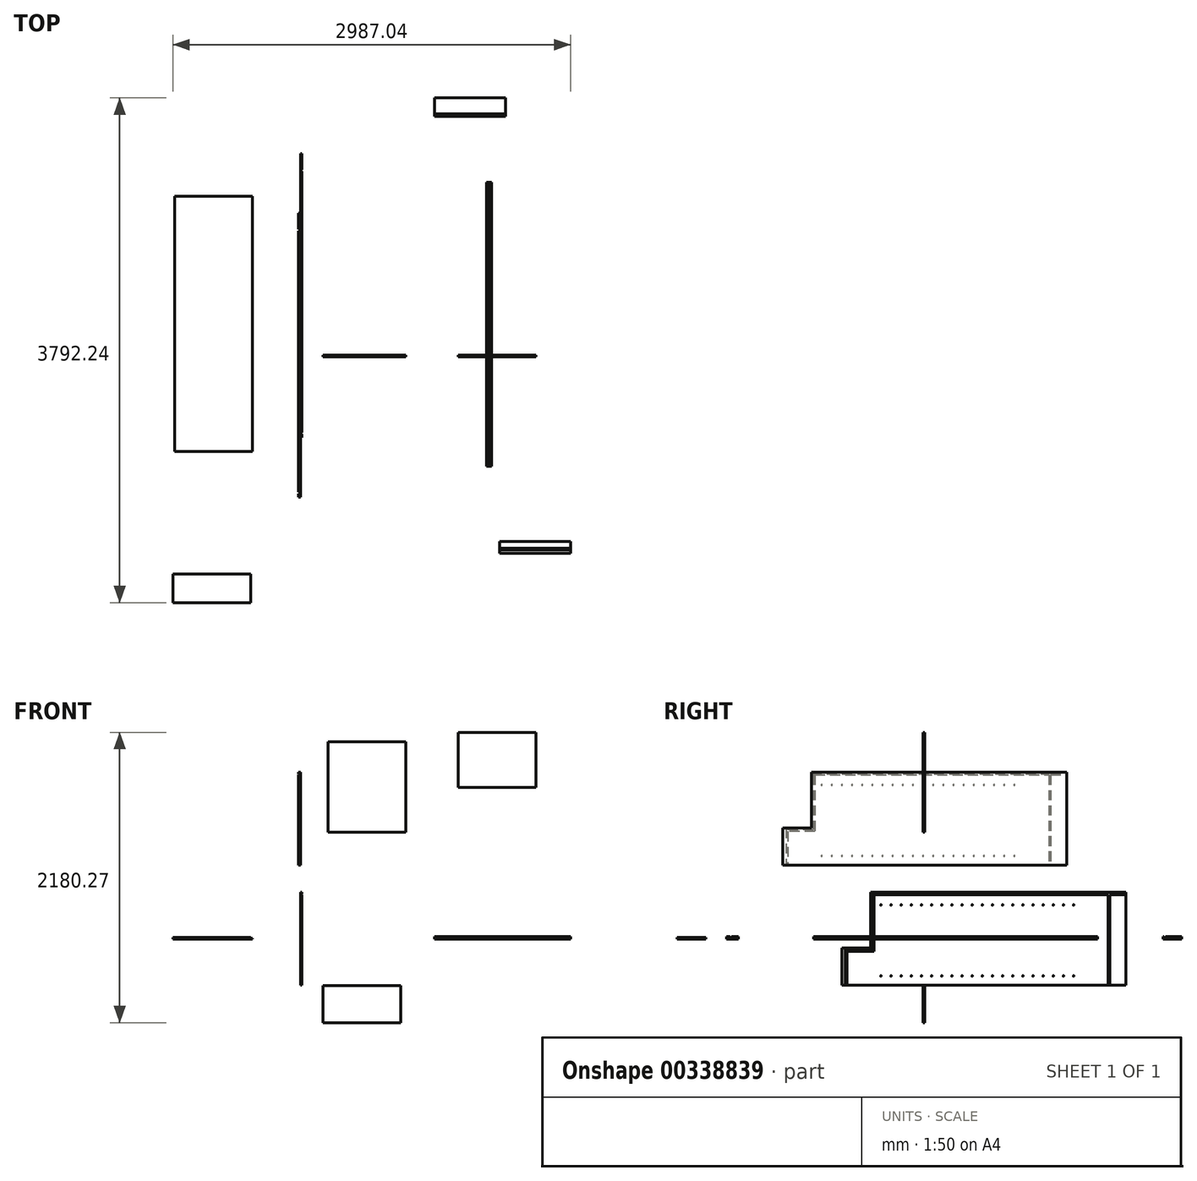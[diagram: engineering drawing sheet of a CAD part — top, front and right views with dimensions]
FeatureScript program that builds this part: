
annotation { "Feature Type Name" : "Feature", "Feature Type Description" : "" }
export const myFeature = defineFeature(function(context is Context, id is Id, definition is map)
    precondition{}
    {
        {
            var Q0;
            Q0=qCreatedBy(makeId("Right.planeOp"),FACE);
            var sketch = newSketch(context, id + "F0", { "sketchPlane" : qUnion([Q0])});
            skLineSegment(sketch, "E0.bottom", {"start": v(-620.38, -346.81) * mm, "end": v(1513.22, -346.81) * mm});
            skLineSegment(sketch, "E0.top", {"start": v(-620.38, 351.69) * mm, "end": v(1513.22, 351.69) * mm});
            skLineSegment(sketch, "E0.left", {"start": v(-620.38, -346.81) * mm, "end": v(-620.38, 351.69) * mm});
            skLineSegment(sketch, "E0.right", {"start": v(1513.22, -346.81) * mm, "end": v(1513.22, 351.69) * mm});
            skSolve(sketch);
        }
        {
            var Q0;
            Q0 = qSketchRegion(id + "F0", true);
            extrude(context, id + "F1", {"entities" : qUnion([Q0]), "depth" : 12.7 * mm});
        }
        {
            var Q0;
            Q0=makeQuery(id+"F1.opExtrude","CAP_FACE",FACE,{"disambiguationData":[OSD([sQuery(id+"F0.wireOp",EDGE,"E0.bottom"),sQuery(id+"F0.wireOp",EDGE,"E0.top"),sQuery(id+"F0.wireOp",EDGE,"E0.left"),sQuery(id+"F0.wireOp",EDGE,"E0.right")])],"isStart":false});
            var sketch = newSketch(context, id + "F2", { "sketchPlane" : qUnion([Q0])});
            skLineSegment(sketch, "E1.0", {"start": v(-620.38, 332.64) * mm, "end": v(1513.22, 332.64) * mm});
            skLineSegment(sketch, "E2.0", {"start": v(-620.38, 338.99) * mm, "end": v(1513.22, 338.99) * mm});
            skLineSegment(sketch, "E3.0", {"start": v(-594.98, -346.81) * mm, "end": v(-594.98, 351.69) * mm});
            skLineSegment(sketch, "E4.0", {"start": v(-582.28, -346.81) * mm, "end": v(-582.28, 351.69) * mm});
            skLineSegment(sketch, "E5.0", {"start": v(1379.87, -346.81) * mm, "end": v(1379.87, 351.69) * mm});
            skLineSegment(sketch, "E6.0", {"start": v(1392.57, -346.81) * mm, "end": v(1392.57, 351.69) * mm});
            skSolve(sketch);
        }
        {
            var Q0;
            Q0 = qSketchRegion(id + "F2", true);
            var Q1;
            {var subQ0=sQuery(id+"F2.wireOp",EDGE,"E5.0");var subQ1=sQuery(id+"F2.wireOp",EDGE,"E2.0");var subQ2=makeQuery(id+"F2.imprint","INTERSECT",VERTEX,{"derivedFrom":[subQ1,subQ0]});Q1=makeQuery(id+"F2.imprint","IMPRINT",FACE,{"disambiguationData":[TD([[makeQuery(id+"F2.imprint","IMPRINT",EDGE,{"disambiguationData":[TD([[subQ2,-1.0]])],"derivedFrom":subQ1}),1.0]])]});}
            var Q2;
            {var subQ0=sQuery(id+"F2.wireOp",EDGE,"E1.0");var subQ1=makeQuery(id+"F1.opExtrude","CAP_EDGE",EDGE,{"disambiguationData":[OSD([sQuery(id+"F0.wireOp",EDGE,"E0.right")])],"isStart":false});var subQ2=makeQuery(id+"F2.imprint","INTERSECT",VERTEX,{"derivedFrom":[subQ1,subQ0]});Q2=makeQuery(id+"F2.imprint","IMPRINT",FACE,{"disambiguationData":[TD([[makeQuery(id+"F2.imprint","IMPRINT",EDGE,{"disambiguationData":[TD([[subQ2,1.0]])],"derivedFrom":subQ0}),1.0]])]});}
            var Q3;
            {var subQ0=sQuery(id+"F2.wireOp",EDGE,"E3.0");var subQ1=sQuery(id+"F2.wireOp",EDGE,"E2.0");var subQ2=makeQuery(id+"F2.imprint","INTERSECT",VERTEX,{"derivedFrom":[subQ1,subQ0]});Q3=makeQuery(id+"F2.imprint","IMPRINT",FACE,{"disambiguationData":[TD([[makeQuery(id+"F2.imprint","IMPRINT",EDGE,{"disambiguationData":[TD([[subQ2,-1.0]])],"derivedFrom":subQ1}),1.0]])]});}
            var Q4;
            {var subQ0=sQuery(id+"F2.wireOp",EDGE,"E1.0");var subQ1=makeQuery(id+"F1.opExtrude","CAP_EDGE",EDGE,{"disambiguationData":[OSD([sQuery(id+"F0.wireOp",EDGE,"E0.left")])],"isStart":false});var subQ2=makeQuery(id+"F2.imprint","INTERSECT",VERTEX,{"derivedFrom":[subQ1,subQ0]});Q4=makeQuery(id+"F2.imprint","IMPRINT",FACE,{"disambiguationData":[TD([[makeQuery(id+"F2.imprint","IMPRINT",EDGE,{"disambiguationData":[TD([[subQ2,-1.0]])],"derivedFrom":subQ0}),1.0]])]});}
            var Q5;
            {var subQ0=sQuery(id+"F2.wireOp",EDGE,"E3.0");var subQ1=sQuery(id+"F2.wireOp",EDGE,"E1.0");var subQ2=makeQuery(id+"F2.imprint","INTERSECT",VERTEX,{"derivedFrom":[subQ1,subQ0]});Q5=makeQuery(id+"F2.imprint","IMPRINT",FACE,{"disambiguationData":[TD([[makeQuery(id+"F2.imprint","IMPRINT",EDGE,{"disambiguationData":[TD([[subQ2,-1.0]])],"derivedFrom":subQ1}),-1.0]])]});}
            var Q6;
            {var subQ0=sQuery(id+"F2.wireOp",EDGE,"E5.0");var subQ1=sQuery(id+"F2.wireOp",EDGE,"E1.0");var subQ2=makeQuery(id+"F2.imprint","INTERSECT",VERTEX,{"derivedFrom":[subQ1,subQ0]});Q6=makeQuery(id+"F2.imprint","IMPRINT",FACE,{"disambiguationData":[TD([[makeQuery(id+"F2.imprint","IMPRINT",EDGE,{"disambiguationData":[TD([[subQ2,-1.0]])],"derivedFrom":subQ1}),-1.0]])]});}
            extrude(context, id + "F3", {"entities" : qUnion([Q0, Q1, Q2, Q3, Q4, Q5, Q6]), "operationType" : NewBodyOperationType.REMOVE, "oppositeDirection" : true, "depth" : 6.35 * mm});
        }
        {
            var Q0;
            {var subQ0=sQuery(id+"F0.wireOp",EDGE,"E0.top");var subQ1=sQuery(id+"F2.wireOp",EDGE,"E4.0");var subQ2=sQuery(id+"F2.wireOp",EDGE,"E2.0");var subQ3=makeQuery(id+"F2.imprint","INTERSECT",VERTEX,{"derivedFrom":[subQ2,subQ1]});Q0=makeQuery(id+"F3.boolean.opBoolean","SPLIT",FACE,{"disambiguationData":[TD([makeQuery(id+"F3.opExtrude","SWEPT_FACE",FACE,{"disambiguationData":[OSD([subQ2]),TDD([makeQuery(id+"F2.imprint","IMPRINT",EDGE,{"disambiguationData":[TD([[subQ3,-1.0]])],"derivedFrom":subQ2})])]})])],"derivedFrom":makeQuery(id+"F1.opExtrude","CAP_FACE",FACE,{"disambiguationData":[OSD([sQuery(id+"F0.wireOp",EDGE,"E0.bottom"),subQ0,sQuery(id+"F0.wireOp",EDGE,"E0.left"),sQuery(id+"F0.wireOp",EDGE,"E0.right")])],"isStart":false})});}
            var sketch = newSketch(context, id + "F4", { "sketchPlane" : qUnion([Q0])});
            skLineSegment(sketch, "E7.0", {"start": v(-582.28, 415.19) * mm, "end": v(1379.87, 415.19) * mm, "construction": true});
            skLineSegment(sketch, "E8.0", {"start": v(-328.28, -327.76) * mm, "end": v(-328.28, 351.69) * mm, "construction": true});
            skCircle(sketch, "E9", {"center": v(-328.28, 415.19) * mm, "radius": 3.17 * mm});
            skCircle(sketch, "E10.0.1.0", {"center": v(-328.28, 948.59) * mm, "radius": 3.17 * mm});
            skCircle(sketch, "E10.1.0.0", {"center": v(-252.08, 415.19) * mm, "radius": 3.17 * mm});
            skCircle(sketch, "E10.1.1.0", {"center": v(-252.08, 948.59) * mm, "radius": 3.17 * mm});
            skCircle(sketch, "E10.2.0.0", {"center": v(-175.88, 415.19) * mm, "radius": 3.17 * mm});
            skCircle(sketch, "E10.2.1.0", {"center": v(-175.88, 948.59) * mm, "radius": 3.17 * mm});
            skCircle(sketch, "E10.3.0.0", {"center": v(-99.68, 415.19) * mm, "radius": 3.17 * mm});
            skCircle(sketch, "E10.3.1.0", {"center": v(-99.68, 948.59) * mm, "radius": 3.17 * mm});
            skCircle(sketch, "E10.4.0.0", {"center": v(-23.48, 415.19) * mm, "radius": 3.17 * mm});
            skCircle(sketch, "E10.4.1.0", {"center": v(-23.48, 948.59) * mm, "radius": 3.17 * mm});
            skCircle(sketch, "E10.5.0.0", {"center": v(52.72, 415.19) * mm, "radius": 3.17 * mm});
            skCircle(sketch, "E10.5.1.0", {"center": v(52.72, 948.59) * mm, "radius": 3.17 * mm});
            skCircle(sketch, "E10.6.0.0", {"center": v(128.92, 415.19) * mm, "radius": 3.17 * mm});
            skCircle(sketch, "E10.6.1.0", {"center": v(128.92, 948.59) * mm, "radius": 3.17 * mm});
            skCircle(sketch, "E10.7.0.0", {"center": v(205.12, 415.19) * mm, "radius": 3.17 * mm});
            skCircle(sketch, "E10.7.1.0", {"center": v(205.12, 948.59) * mm, "radius": 3.17 * mm});
            skCircle(sketch, "E10.8.0.0", {"center": v(281.32, 415.19) * mm, "radius": 3.17 * mm});
            skCircle(sketch, "E10.8.1.0", {"center": v(281.32, 948.59) * mm, "radius": 3.17 * mm});
            skCircle(sketch, "E10.9.0.0", {"center": v(357.52, 415.19) * mm, "radius": 3.17 * mm});
            skCircle(sketch, "E10.9.1.0", {"center": v(357.52, 948.59) * mm, "radius": 3.17 * mm});
            skCircle(sketch, "E10.10.0.0", {"center": v(433.72, 415.19) * mm, "radius": 3.17 * mm});
            skCircle(sketch, "E10.10.1.0", {"center": v(433.72, 948.59) * mm, "radius": 3.17 * mm});
            skCircle(sketch, "E10.11.0.0", {"center": v(509.92, 415.19) * mm, "radius": 3.17 * mm});
            skCircle(sketch, "E10.11.1.0", {"center": v(509.92, 948.59) * mm, "radius": 3.17 * mm});
            skCircle(sketch, "E10.12.0.0", {"center": v(586.12, 415.19) * mm, "radius": 3.17 * mm});
            skCircle(sketch, "E10.12.1.0", {"center": v(586.12, 948.59) * mm, "radius": 3.17 * mm});
            skCircle(sketch, "E10.13.0.0", {"center": v(662.32, 415.19) * mm, "radius": 3.17 * mm});
            skCircle(sketch, "E10.13.1.0", {"center": v(662.32, 948.59) * mm, "radius": 3.17 * mm});
            skCircle(sketch, "E10.14.0.0", {"center": v(738.52, 415.19) * mm, "radius": 3.17 * mm});
            skCircle(sketch, "E10.14.1.0", {"center": v(738.52, 948.59) * mm, "radius": 3.17 * mm});
            skCircle(sketch, "E10.15.0.0", {"center": v(814.72, 415.19) * mm, "radius": 3.17 * mm});
            skCircle(sketch, "E10.15.1.0", {"center": v(814.72, 948.59) * mm, "radius": 3.17 * mm});
            skCircle(sketch, "E10.16.0.0", {"center": v(890.92, 415.19) * mm, "radius": 3.17 * mm});
            skCircle(sketch, "E10.16.1.0", {"center": v(890.92, 948.59) * mm, "radius": 3.17 * mm});
            skCircle(sketch, "E10.17.0.0", {"center": v(967.12, 415.19) * mm, "radius": 3.17 * mm});
            skCircle(sketch, "E10.17.1.0", {"center": v(967.12, 948.59) * mm, "radius": 3.17 * mm});
            skCircle(sketch, "E10.18.0.0", {"center": v(1043.32, 415.19) * mm, "radius": 3.17 * mm});
            skCircle(sketch, "E10.18.1.0", {"center": v(1043.32, 948.59) * mm, "radius": 3.17 * mm});
            skCircle(sketch, "E10.19.0.0", {"center": v(1119.52, 415.19) * mm, "radius": 3.17 * mm});
            skCircle(sketch, "E10.19.1.0", {"center": v(1119.52, 948.59) * mm, "radius": 3.17 * mm});
            skLineSegment(sketch, "E10.direction1", {"start": v(-328.28, 415.19) * mm, "end": v(-252.08, 415.19) * mm, "construction": true});
            skLineSegment(sketch, "E10.direction2", {"start": v(-328.28, 415.19) * mm, "end": v(-328.28, 948.59) * mm, "construction": true});
            skSolve(sketch);
        }
        {
            var Q0;
            Q0 = qSketchRegion(id + "F4", true);
            extrude(context, id + "F5", {"entities" : qUnion([Q0]), "operationType" : NewBodyOperationType.REMOVE, "oppositeDirection" : true, "depth" : 9.52 * mm});
        }
        {
            var Q0;
            Q0=makeQuery(id+"F1.opExtrude","CAP_FACE",FACE,{"disambiguationData":[OSD([sQuery(id+"F0.wireOp",EDGE,"E0.bottom"),sQuery(id+"F0.wireOp",EDGE,"E0.top"),sQuery(id+"F0.wireOp",EDGE,"E0.left"),sQuery(id+"F0.wireOp",EDGE,"E0.right")])],"isStart":true});
            var sketch = newSketch(context, id + "F6", { "sketchPlane" : qUnion([Q0])});
            skLineSegment(sketch, "E11.bottom", {"start": v(1065.98, 1252.71) * mm, "end": v(-1067.62, 1252.71) * mm});
            skLineSegment(sketch, "E11.top", {"start": v(1065.98, 554.21) * mm, "end": v(-1067.62, 554.21) * mm});
            skLineSegment(sketch, "E11.left", {"start": v(1065.98, 1252.71) * mm, "end": v(1065.98, 554.21) * mm});
            skLineSegment(sketch, "E11.right", {"start": v(-1067.62, 1252.71) * mm, "end": v(-1067.62, 554.21) * mm});
            skSolve(sketch);
        }
        {
            var Q0;
            Q0 = qSketchRegion(id + "F6", true);
            extrude(context, id + "F7", {"entities" : qUnion([Q0]), "depth" : 12.7 * mm});
        }
        {
            var Q0;
            Q0=makeQuery(id+"F7.opExtrude","CAP_FACE",FACE,{"disambiguationData":[OSD([sQuery(id+"F6.wireOp",EDGE,"E11.bottom"),sQuery(id+"F6.wireOp",EDGE,"E11.top"),sQuery(id+"F6.wireOp",EDGE,"E11.left"),sQuery(id+"F6.wireOp",EDGE,"E11.right")])],"isStart":false});
            var sketch = newSketch(context, id + "F8", { "sketchPlane" : qUnion([Q0])});
            skLineSegment(sketch, "E12.0", {"start": v(1065.98, 1240.01) * mm, "end": v(-1067.62, 1240.01) * mm});
            skLineSegment(sketch, "E13.0", {"start": v(1065.98, 1233.66) * mm, "end": v(-1067.62, 1233.66) * mm});
            skLineSegment(sketch, "E14.0", {"start": v(-934.27, 1252.71) * mm, "end": v(-934.27, 554.21) * mm});
            skLineSegment(sketch, "E15.0", {"start": v(-946.97, 1252.71) * mm, "end": v(-946.97, 554.21) * mm});
            skLineSegment(sketch, "E16.0", {"start": v(1040.58, 1252.71) * mm, "end": v(1040.58, 554.21) * mm});
            skLineSegment(sketch, "E17.0", {"start": v(1027.88, 1252.71) * mm, "end": v(1027.88, 554.21) * mm});
            skSolve(sketch);
        }
        {
            var Q0;
            {var subQ0=sQuery(id+"F8.wireOp",EDGE,"E16.0");var subQ1=sQuery(id+"F8.wireOp",EDGE,"E13.0");var subQ2=makeQuery(id+"F8.imprint","INTERSECT",VERTEX,{"derivedFrom":[subQ1,subQ0]});Q0=makeQuery(id+"F8.imprint","IMPRINT",FACE,{"disambiguationData":[TD([[makeQuery(id+"F8.imprint","IMPRINT",EDGE,{"disambiguationData":[TD([[subQ2,-1.0]])],"derivedFrom":subQ1}),1.0]])]});}
            var Q1;
            {var subQ0=sQuery(id+"F8.wireOp",EDGE,"E16.0");var subQ1=sQuery(id+"F8.wireOp",EDGE,"E12.0");var subQ2=makeQuery(id+"F8.imprint","INTERSECT",VERTEX,{"derivedFrom":[subQ1,subQ0]});Q1=makeQuery(id+"F8.imprint","IMPRINT",FACE,{"disambiguationData":[TD([[makeQuery(id+"F8.imprint","IMPRINT",EDGE,{"disambiguationData":[TD([[subQ2,-1.0]])],"derivedFrom":subQ1}),-1.0]])]});}
            var Q2;
            {var subQ0=sQuery(id+"F8.wireOp",EDGE,"E17.0");var subQ1=sQuery(id+"F8.wireOp",EDGE,"E12.0");var subQ2=makeQuery(id+"F8.imprint","INTERSECT",VERTEX,{"derivedFrom":[subQ1,subQ0]});Q2=makeQuery(id+"F8.imprint","IMPRINT",FACE,{"disambiguationData":[TD([[makeQuery(id+"F8.imprint","IMPRINT",EDGE,{"disambiguationData":[TD([[subQ2,-1.0]])],"derivedFrom":subQ1}),1.0]])]});}
            var Q3;
            {var subQ0=sQuery(id+"F8.wireOp",EDGE,"E12.0");var subQ1=makeQuery(id+"F7.opExtrude","CAP_EDGE",EDGE,{"disambiguationData":[OSD([sQuery(id+"F6.wireOp",EDGE,"E11.left")])],"isStart":false});var subQ2=makeQuery(id+"F8.imprint","INTERSECT",VERTEX,{"derivedFrom":[subQ1,subQ0]});Q3=makeQuery(id+"F8.imprint","IMPRINT",FACE,{"disambiguationData":[TD([[makeQuery(id+"F8.imprint","IMPRINT",EDGE,{"disambiguationData":[TD([[subQ2,-1.0]])],"derivedFrom":subQ0}),1.0]])]});}
            var Q4;
            {var subQ0=sQuery(id+"F8.wireOp",EDGE,"E14.0");var subQ1=sQuery(id+"F8.wireOp",EDGE,"E12.0");var subQ2=makeQuery(id+"F8.imprint","INTERSECT",VERTEX,{"derivedFrom":[subQ1,subQ0]});Q4=makeQuery(id+"F8.imprint","IMPRINT",FACE,{"disambiguationData":[TD([[makeQuery(id+"F8.imprint","IMPRINT",EDGE,{"disambiguationData":[TD([[subQ2,-1.0]])],"derivedFrom":subQ1}),-1.0]])]});}
            var Q5;
            {var subQ0=sQuery(id+"F8.wireOp",EDGE,"E14.0");var subQ1=sQuery(id+"F8.wireOp",EDGE,"E13.0");var subQ2=makeQuery(id+"F8.imprint","INTERSECT",VERTEX,{"derivedFrom":[subQ1,subQ0]});Q5=makeQuery(id+"F8.imprint","IMPRINT",FACE,{"disambiguationData":[TD([[makeQuery(id+"F8.imprint","IMPRINT",EDGE,{"disambiguationData":[TD([[subQ2,-1.0]])],"derivedFrom":subQ1}),1.0]])]});}
            var Q6;
            {var subQ0=sQuery(id+"F8.wireOp",EDGE,"E12.0");var subQ1=makeQuery(id+"F7.opExtrude","CAP_EDGE",EDGE,{"disambiguationData":[OSD([sQuery(id+"F6.wireOp",EDGE,"E11.right")])],"isStart":false});var subQ2=makeQuery(id+"F8.imprint","INTERSECT",VERTEX,{"derivedFrom":[subQ1,subQ0]});Q6=makeQuery(id+"F8.imprint","IMPRINT",FACE,{"disambiguationData":[TD([[makeQuery(id+"F8.imprint","IMPRINT",EDGE,{"disambiguationData":[TD([[subQ2,1.0]])],"derivedFrom":subQ0}),1.0]])]});}
            var Q7;
            {var subQ0=sQuery(id+"F8.wireOp",EDGE,"E14.0");var subQ1=sQuery(id+"F8.wireOp",EDGE,"E12.0");var subQ2=makeQuery(id+"F8.imprint","INTERSECT",VERTEX,{"derivedFrom":[subQ1,subQ0]});Q7=makeQuery(id+"F8.imprint","IMPRINT",FACE,{"disambiguationData":[TD([[makeQuery(id+"F8.imprint","IMPRINT",EDGE,{"disambiguationData":[TD([[subQ2,-1.0]])],"derivedFrom":subQ1}),1.0]])]});}
            var Q8;
            {var subQ0=sQuery(id+"F8.wireOp",EDGE,"E16.0");var subQ1=sQuery(id+"F8.wireOp",EDGE,"E12.0");var subQ2=makeQuery(id+"F8.imprint","INTERSECT",VERTEX,{"derivedFrom":[subQ1,subQ0]});Q8=makeQuery(id+"F8.imprint","IMPRINT",FACE,{"disambiguationData":[TD([[makeQuery(id+"F8.imprint","IMPRINT",EDGE,{"disambiguationData":[TD([[subQ2,-1.0]])],"derivedFrom":subQ1}),1.0]])]});}
            extrude(context, id + "F9", {"entities" : qUnion([Q0, Q1, Q2, Q3, Q4, Q5, Q6, Q7, Q8]), "operationType" : NewBodyOperationType.REMOVE, "oppositeDirection" : true, "depth" : 6.35 * mm});
        }
        {
            var Q0;
            {var subQ0=sQuery(id+"F6.wireOp",EDGE,"E11.top");var subQ1=sQuery(id+"F8.wireOp",EDGE,"E17.0");var subQ3=sQuery(id+"F8.wireOp",EDGE,"E13.0");var subQ4=makeQuery(id+"F8.imprint","INTERSECT",VERTEX,{"derivedFrom":[subQ3,subQ1]});Q0=makeQuery(id+"F9.boolean.opBoolean","SPLIT",FACE,{"disambiguationData":[TD([makeQuery(id+"F9.opExtrude","SWEPT_FACE",FACE,{"disambiguationData":[OSD([subQ3]),TDD([makeQuery(id+"F8.imprint","IMPRINT",EDGE,{"disambiguationData":[TD([[subQ4,-1.0]])],"derivedFrom":subQ3})])]})])],"derivedFrom":makeQuery(id+"F7.opExtrude","CAP_FACE",FACE,{"disambiguationData":[OSD([sQuery(id+"F6.wireOp",EDGE,"E11.bottom"),subQ0,sQuery(id+"F6.wireOp",EDGE,"E11.left"),sQuery(id+"F6.wireOp",EDGE,"E11.right")])],"isStart":false})});}
            var sketch = newSketch(context, id + "F10", { "sketchPlane" : qUnion([Q0])});
            skLineSegment(sketch, "E18.0", {"start": v(1027.88, 1157.46) * mm, "end": v(-934.27, 1157.46) * mm, "construction": true});
            skLineSegment(sketch, "E19.0", {"start": v(773.88, 1233.66) * mm, "end": v(773.88, 554.21) * mm, "construction": true});
            skCircle(sketch, "E20", {"center": v(773.88, 1157.46) * mm, "radius": 3.17 * mm});
            skCircle(sketch, "E21.0.1.0", {"center": v(773.88, 624.06) * mm, "radius": 3.17 * mm});
            skCircle(sketch, "E21.1.0.0", {"center": v(697.68, 1157.46) * mm, "radius": 3.17 * mm});
            skCircle(sketch, "E21.1.1.0", {"center": v(697.68, 624.06) * mm, "radius": 3.17 * mm});
            skCircle(sketch, "E21.2.0.0", {"center": v(621.48, 1157.46) * mm, "radius": 3.17 * mm});
            skCircle(sketch, "E21.2.1.0", {"center": v(621.48, 624.06) * mm, "radius": 3.17 * mm});
            skCircle(sketch, "E21.3.0.0", {"center": v(545.28, 1157.46) * mm, "radius": 3.17 * mm});
            skCircle(sketch, "E21.3.1.0", {"center": v(545.28, 624.06) * mm, "radius": 3.17 * mm});
            skCircle(sketch, "E21.4.0.0", {"center": v(469.08, 1157.46) * mm, "radius": 3.17 * mm});
            skCircle(sketch, "E21.4.1.0", {"center": v(469.08, 624.06) * mm, "radius": 3.17 * mm});
            skCircle(sketch, "E21.5.0.0", {"center": v(392.88, 1157.46) * mm, "radius": 3.17 * mm});
            skCircle(sketch, "E21.5.1.0", {"center": v(392.88, 624.06) * mm, "radius": 3.17 * mm});
            skCircle(sketch, "E21.6.0.0", {"center": v(316.68, 1157.46) * mm, "radius": 3.17 * mm});
            skCircle(sketch, "E21.6.1.0", {"center": v(316.68, 624.06) * mm, "radius": 3.17 * mm});
            skCircle(sketch, "E21.7.0.0", {"center": v(240.48, 1157.46) * mm, "radius": 3.17 * mm});
            skCircle(sketch, "E21.7.1.0", {"center": v(240.48, 624.06) * mm, "radius": 3.17 * mm});
            skCircle(sketch, "E21.8.0.0", {"center": v(164.28, 1157.46) * mm, "radius": 3.17 * mm});
            skCircle(sketch, "E21.8.1.0", {"center": v(164.28, 624.06) * mm, "radius": 3.17 * mm});
            skCircle(sketch, "E21.9.0.0", {"center": v(88.08, 1157.46) * mm, "radius": 3.17 * mm});
            skCircle(sketch, "E21.9.1.0", {"center": v(88.08, 624.06) * mm, "radius": 3.17 * mm});
            skCircle(sketch, "E21.10.0.0", {"center": v(11.88, 1157.46) * mm, "radius": 3.17 * mm});
            skCircle(sketch, "E21.10.1.0", {"center": v(11.88, 624.06) * mm, "radius": 3.17 * mm});
            skCircle(sketch, "E21.11.0.0", {"center": v(-64.32, 1157.46) * mm, "radius": 3.17 * mm});
            skCircle(sketch, "E21.11.1.0", {"center": v(-64.32, 624.06) * mm, "radius": 3.17 * mm});
            skCircle(sketch, "E21.12.0.0", {"center": v(-140.52, 1157.46) * mm, "radius": 3.17 * mm});
            skCircle(sketch, "E21.12.1.0", {"center": v(-140.52, 624.06) * mm, "radius": 3.17 * mm});
            skCircle(sketch, "E21.13.0.0", {"center": v(-216.72, 1157.46) * mm, "radius": 3.17 * mm});
            skCircle(sketch, "E21.13.1.0", {"center": v(-216.72, 624.06) * mm, "radius": 3.17 * mm});
            skCircle(sketch, "E21.14.0.0", {"center": v(-292.92, 1157.46) * mm, "radius": 3.17 * mm});
            skCircle(sketch, "E21.14.1.0", {"center": v(-292.92, 624.06) * mm, "radius": 3.17 * mm});
            skCircle(sketch, "E21.15.0.0", {"center": v(-369.12, 1157.46) * mm, "radius": 3.17 * mm});
            skCircle(sketch, "E21.15.1.0", {"center": v(-369.12, 624.06) * mm, "radius": 3.17 * mm});
            skCircle(sketch, "E21.16.0.0", {"center": v(-445.32, 1157.46) * mm, "radius": 3.17 * mm});
            skCircle(sketch, "E21.16.1.0", {"center": v(-445.32, 624.06) * mm, "radius": 3.17 * mm});
            skCircle(sketch, "E21.17.0.0", {"center": v(-521.52, 1157.46) * mm, "radius": 3.17 * mm});
            skCircle(sketch, "E21.17.1.0", {"center": v(-521.52, 624.06) * mm, "radius": 3.17 * mm});
            skCircle(sketch, "E21.18.0.0", {"center": v(-597.72, 1157.46) * mm, "radius": 3.17 * mm});
            skCircle(sketch, "E21.18.1.0", {"center": v(-597.72, 624.06) * mm, "radius": 3.17 * mm});
            skCircle(sketch, "E21.19.0.0", {"center": v(-673.92, 1157.46) * mm, "radius": 3.17 * mm});
            skCircle(sketch, "E21.19.1.0", {"center": v(-673.92, 624.06) * mm, "radius": 3.17 * mm});
            skLineSegment(sketch, "E21.direction1", {"start": v(773.88, 1157.46) * mm, "end": v(697.68, 1157.46) * mm, "construction": true});
            skLineSegment(sketch, "E21.direction2", {"start": v(773.88, 1157.46) * mm, "end": v(773.88, 624.06) * mm, "construction": true});
            skSolve(sketch);
        }
        {
            var Q0;
            Q0 = qSketchRegion(id + "F10", true);
            extrude(context, id + "F11", {"entities" : qUnion([Q0]), "operationType" : NewBodyOperationType.REMOVE, "oppositeDirection" : true, "depth" : 9.52 * mm});
        }
        {
            var Q0;
            Q0=qCreatedBy(makeId("Front.planeOp"),FACE);
            var sketch = newSketch(context, id + "F12", { "sketchPlane" : qUnion([Q0])});
            skLineSegment(sketch, "E22.bottom", {"start": v(790.64, 1483.5) * mm, "end": v(206.44, 1483.5) * mm});
            skLineSegment(sketch, "E22.top", {"start": v(790.64, 804.06) * mm, "end": v(206.44, 804.06) * mm});
            skLineSegment(sketch, "E22.left", {"start": v(790.64, 1483.5) * mm, "end": v(790.64, 804.06) * mm});
            skLineSegment(sketch, "E22.right", {"start": v(206.44, 1483.5) * mm, "end": v(206.44, 804.06) * mm});
            skSolve(sketch);
        }
        {
            var Q0;
            Q0 = qSketchRegion(id + "F12", true);
            extrude(context, id + "F13", {"entities" : qUnion([Q0]), "depth" : 12.7 * mm});
        }
        {
            var Q0;
            Q0=qCreatedBy(makeId("Top.planeOp"),FACE);
            var sketch = newSketch(context, id + "F14", { "sketchPlane" : qUnion([Q0])});
            skLineSegment(sketch, "E23.bottom", {"start": v(-360.37, -724.51) * mm, "end": v(-944.57, -724.51) * mm});
            skLineSegment(sketch, "E23.top", {"start": v(-360.37, 1193.19) * mm, "end": v(-944.57, 1193.19) * mm});
            skLineSegment(sketch, "E23.left", {"start": v(-360.37, -724.51) * mm, "end": v(-360.37, 1193.19) * mm});
            skLineSegment(sketch, "E23.right", {"start": v(-944.57, -724.51) * mm, "end": v(-944.57, 1193.19) * mm});
            skSolve(sketch);
        }
        {
            var Q0;
            Q0 = qSketchRegion(id + "F14", true);
            extrude(context, id + "F15", {"entities" : qUnion([Q0]), "depth" : 6.35 * mm});
        }
        {
            var Q0;
            Q0=qCreatedBy(makeId("Top.planeOp"),FACE);
            var sketch = newSketch(context, id + "F16", { "sketchPlane" : qUnion([Q0])});
            skLineSegment(sketch, "E24.bottom", {"start": v(1436.27, -833.85) * mm, "end": v(1398.17, -833.85) * mm});
            skLineSegment(sketch, "E24.top", {"start": v(1436.27, 1299.75) * mm, "end": v(1398.17, 1299.75) * mm});
            skLineSegment(sketch, "E24.left", {"start": v(1436.27, -833.85) * mm, "end": v(1436.27, 1299.75) * mm});
            skLineSegment(sketch, "E24.right", {"start": v(1398.17, -833.85) * mm, "end": v(1398.17, 1299.75) * mm});
            skLineSegment(sketch, "E25.bottom", {"start": v(1542.63, 1792.16) * mm, "end": v(1009.23, 1792.16) * mm});
            skLineSegment(sketch, "E25.top", {"start": v(1542.63, 1931.86) * mm, "end": v(1009.23, 1931.86) * mm});
            skLineSegment(sketch, "E25.left", {"start": v(1542.63, 1792.16) * mm, "end": v(1542.63, 1931.86) * mm});
            skLineSegment(sketch, "E25.right", {"start": v(1009.23, 1792.16) * mm, "end": v(1009.23, 1931.86) * mm});
            skLineSegment(sketch, "E26.bottom", {"start": v(2030.11, -1487.93) * mm, "end": v(1496.71, -1487.93) * mm});
            skLineSegment(sketch, "E26.top", {"start": v(2030.11, -1399.03) * mm, "end": v(1496.71, -1399.03) * mm});
            skLineSegment(sketch, "E26.left", {"start": v(2030.11, -1487.93) * mm, "end": v(2030.11, -1399.03) * mm});
            skLineSegment(sketch, "E26.right", {"start": v(1496.71, -1487.93) * mm, "end": v(1496.71, -1399.03) * mm});
            skSolve(sketch);
        }
        {
            var Q0;
            Q0 = qSketchRegion(id + "F16", true);
            extrude(context, id + "F17", {"entities" : qUnion([Q0]), "depth" : 19.05 * mm});
        }
        {
            var Q0;
            {var subQ0=sQuery(id+"F6.wireOp",EDGE,"E11.bottom");var subQ2=sQuery(id+"F8.wireOp",EDGE,"E12.0");var subQ4=sQuery(id+"F6.wireOp",EDGE,"E11.left");Q0=makeQuery(id+"F9.boolean.opBoolean","SPLIT",FACE,{"disambiguationData":[TD([makeQuery(id+"F9.opExtrude","SWEPT_FACE",FACE,{"disambiguationData":[OSD([subQ2]),TDD([makeQuery(id+"F8.imprint","IMPRINT",EDGE,{"disambiguationData":[TD([[makeQuery(id+"F8.imprint","INTERSECT",VERTEX,{"derivedFrom":[makeQuery(id+"F7.opExtrude","CAP_EDGE",EDGE,{"disambiguationData":[OSD([subQ4])],"isStart":false}),subQ2]}),-1.0]])],"derivedFrom":subQ2})])]})])],"derivedFrom":makeQuery(id+"F7.opExtrude","CAP_FACE",FACE,{"disambiguationData":[OSD([subQ0,sQuery(id+"F6.wireOp",EDGE,"E11.top"),subQ4,sQuery(id+"F6.wireOp",EDGE,"E11.right")])],"isStart":false})});}
            var sketch = newSketch(context, id + "F18", { "sketchPlane" : qUnion([Q0])});
            skLineSegment(sketch, "E27.bottom", {"start": v(1065.98, 1252.71) * mm, "end": v(850.08, 1252.71) * mm});
            skLineSegment(sketch, "E27.top", {"start": v(1065.98, 833.61) * mm, "end": v(850.08, 833.61) * mm});
            skLineSegment(sketch, "E27.left", {"start": v(1065.98, 1252.71) * mm, "end": v(1065.98, 833.61) * mm});
            skLineSegment(sketch, "E27.right", {"start": v(850.08, 1252.71) * mm, "end": v(850.08, 833.61) * mm});
            skSolve(sketch);
        }
        {
            var Q0;
            Q0 = qSketchRegion(id + "F18", true);
            extrude(context, id + "F19", {"entities" : qUnion([Q0]), "operationType" : NewBodyOperationType.REMOVE, "oppositeDirection" : true, "depth" : 12.7 * mm});
        }
        {
            var Q0;
            {var subQ0=sQuery(id+"F6.wireOp",EDGE,"E11.top");var subQ1=sQuery(id+"F8.wireOp",EDGE,"E17.0");var subQ3=sQuery(id+"F8.wireOp",EDGE,"E13.0");var subQ4=makeQuery(id+"F8.imprint","INTERSECT",VERTEX,{"derivedFrom":[subQ3,subQ1]});Q0=makeQuery(id+"F9.boolean.opBoolean","SPLIT",FACE,{"disambiguationData":[TD([makeQuery(id+"F9.opExtrude","SWEPT_FACE",FACE,{"disambiguationData":[OSD([subQ3]),TDD([makeQuery(id+"F8.imprint","IMPRINT",EDGE,{"disambiguationData":[TD([[subQ4,-1.0]])],"derivedFrom":subQ3})])]})])],"derivedFrom":makeQuery(id+"F7.opExtrude","CAP_FACE",FACE,{"disambiguationData":[OSD([sQuery(id+"F6.wireOp",EDGE,"E11.bottom"),subQ0,sQuery(id+"F6.wireOp",EDGE,"E11.left"),sQuery(id+"F6.wireOp",EDGE,"E11.right")])],"isStart":false})});}
            var sketch = newSketch(context, id + "F20", { "sketchPlane" : qUnion([Q0])});
            skLineSegment(sketch, "E28", {"start": v(837.38, 1233.66) * mm, "end": v(837.38, 820.91) * mm});
            skLineSegment(sketch, "E29", {"start": v(837.38, 820.91) * mm, "end": v(1027.88, 820.91) * mm});
            skLineSegment(sketch, "E30.0", {"start": v(824.68, 1233.66) * mm, "end": v(824.68, 808.21) * mm});
            skLineSegment(sketch, "E31.0", {"start": v(824.68, 808.21) * mm, "end": v(1027.88, 808.21) * mm});
            skSolve(sketch);
        }
        {
            var Q0;
            {var subQ3=sQuery(id+"F20.wireOp",EDGE,"E28");Q0=makeQuery(id+"F20.imprint","IMPRINT",FACE,{"disambiguationData":[TD([[makeQuery(id+"F20.imprint","IMPRINT",EDGE,{"derivedFrom":subQ3}),-1.0]])]});}
            extrude(context, id + "F21", {"entities" : qUnion([Q0]), "operationType" : NewBodyOperationType.REMOVE, "oppositeDirection" : true, "depth" : 6.35 * mm});
        }
        {
            var Q0;
            Q0=qCreatedBy(makeId("Front.planeOp"),FACE);
            var sketch = newSketch(context, id + "F22", { "sketchPlane" : qUnion([Q0])});
            skLineSegment(sketch, "E32.bottom", {"start": v(1768.66, 1552.5) * mm, "end": v(1184.46, 1552.5) * mm});
            skLineSegment(sketch, "E32.top", {"start": v(1768.66, 1139.75) * mm, "end": v(1184.46, 1139.75) * mm});
            skLineSegment(sketch, "E32.left", {"start": v(1768.66, 1552.5) * mm, "end": v(1768.66, 1139.75) * mm});
            skLineSegment(sketch, "E32.right", {"start": v(1184.46, 1552.5) * mm, "end": v(1184.46, 1139.75) * mm});
            skSolve(sketch);
        }
        {
            var Q0;
            Q0 = qSketchRegion(id + "F22", true);
            extrude(context, id + "F23", {"entities" : qUnion([Q0]), "depth" : 12.7 * mm});
        }
        {
            var Q0;
            Q0=qCreatedBy(makeId("Top.planeOp"),FACE);
            var sketch = newSketch(context, id + "F24", { "sketchPlane" : qUnion([Q0])});
            skLineSegment(sketch, "E33.bottom", {"start": v(-956.93, -1860.38) * mm, "end": v(-372.73, -1860.38) * mm});
            skLineSegment(sketch, "E33.top", {"start": v(-956.93, -1644.48) * mm, "end": v(-372.73, -1644.48) * mm});
            skLineSegment(sketch, "E33.left", {"start": v(-956.93, -1860.38) * mm, "end": v(-956.93, -1644.48) * mm});
            skLineSegment(sketch, "E33.right", {"start": v(-372.73, -1860.38) * mm, "end": v(-372.73, -1644.48) * mm});
            skSolve(sketch);
        }
        {
            var Q0;
            Q0=makeQuery(id+"F24.imprint","IMPRINT",FACE,{"disambiguationData":[TD([[makeQuery(id+"F24.imprint","IMPRINT",EDGE,{"derivedFrom":sQuery(id+"F24.wireOp",EDGE,"E33.bottom")}),1.0]])]});
            extrude(context, id + "F25", {"entities" : qUnion([Q0]), "depth" : 12.7 * mm});
        }
        {
            var Q0;
            {var subQ0=sQuery(id+"F0.wireOp",EDGE,"E0.bottom");var subQ3=sQuery(id+"F2.wireOp",EDGE,"E1.0");var subQ5=sQuery(id+"F2.wireOp",EDGE,"E4.0");var subQ6=makeQuery(id+"F2.imprint","INTERSECT",VERTEX,{"derivedFrom":[subQ3,subQ5]});Q0=makeQuery(id+"F3.boolean.opBoolean","SPLIT",FACE,{"disambiguationData":[TD([makeQuery(id+"F3.opExtrude","SWEPT_FACE",FACE,{"disambiguationData":[OSD([subQ3]),TDD([makeQuery(id+"F2.imprint","IMPRINT",EDGE,{"disambiguationData":[TD([[subQ6,-1.0]])],"derivedFrom":subQ3})])]})])],"derivedFrom":makeQuery(id+"F1.opExtrude","CAP_FACE",FACE,{"disambiguationData":[OSD([subQ0,sQuery(id+"F0.wireOp",EDGE,"E0.top"),sQuery(id+"F0.wireOp",EDGE,"E0.left"),sQuery(id+"F0.wireOp",EDGE,"E0.right")])],"isStart":false})});}
            var sketch = newSketch(context, id + "F26", { "sketchPlane" : qUnion([Q0])});
            skLineSegment(sketch, "E34.0", {"start": v(-328.28, -346.81) * mm, "end": v(-328.28, 332.64) * mm, "construction": true});
            skLineSegment(sketch, "E35.0", {"start": v(-582.28, 256.44) * mm, "end": v(1379.87, 256.44) * mm, "construction": true});
            skCircle(sketch, "E36", {"center": v(-328.28, 256.44) * mm, "radius": 3.18 * mm});
            skCircle(sketch, "E37.0.1.0", {"center": v(-328.28, -276.96) * mm, "radius": 3.18 * mm});
            skCircle(sketch, "E37.1.0.0", {"center": v(-252.08, 256.44) * mm, "radius": 3.18 * mm});
            skCircle(sketch, "E37.1.1.0", {"center": v(-252.08, -276.96) * mm, "radius": 3.18 * mm});
            skCircle(sketch, "E37.2.0.0", {"center": v(-175.88, 256.44) * mm, "radius": 3.18 * mm});
            skCircle(sketch, "E37.2.1.0", {"center": v(-175.88, -276.96) * mm, "radius": 3.18 * mm});
            skCircle(sketch, "E37.3.0.0", {"center": v(-99.68, 256.44) * mm, "radius": 3.18 * mm});
            skCircle(sketch, "E37.3.1.0", {"center": v(-99.68, -276.96) * mm, "radius": 3.18 * mm});
            skCircle(sketch, "E37.4.0.0", {"center": v(-23.48, 256.44) * mm, "radius": 3.18 * mm});
            skCircle(sketch, "E37.4.1.0", {"center": v(-23.48, -276.96) * mm, "radius": 3.18 * mm});
            skCircle(sketch, "E37.5.0.0", {"center": v(52.72, 256.44) * mm, "radius": 3.18 * mm});
            skCircle(sketch, "E37.5.1.0", {"center": v(52.72, -276.96) * mm, "radius": 3.18 * mm});
            skCircle(sketch, "E37.6.0.0", {"center": v(128.92, 256.44) * mm, "radius": 3.18 * mm});
            skCircle(sketch, "E37.6.1.0", {"center": v(128.92, -276.96) * mm, "radius": 3.18 * mm});
            skCircle(sketch, "E37.7.0.0", {"center": v(205.12, 256.44) * mm, "radius": 3.18 * mm});
            skCircle(sketch, "E37.7.1.0", {"center": v(205.12, -276.96) * mm, "radius": 3.18 * mm});
            skCircle(sketch, "E37.8.0.0", {"center": v(281.32, 256.44) * mm, "radius": 3.18 * mm});
            skCircle(sketch, "E37.8.1.0", {"center": v(281.32, -276.96) * mm, "radius": 3.18 * mm});
            skCircle(sketch, "E37.9.0.0", {"center": v(357.52, 256.44) * mm, "radius": 3.18 * mm});
            skCircle(sketch, "E37.9.1.0", {"center": v(357.52, -276.96) * mm, "radius": 3.18 * mm});
            skCircle(sketch, "E37.10.0.0", {"center": v(433.72, 256.44) * mm, "radius": 3.18 * mm});
            skCircle(sketch, "E37.10.1.0", {"center": v(433.72, -276.96) * mm, "radius": 3.18 * mm});
            skCircle(sketch, "E37.11.0.0", {"center": v(509.92, 256.44) * mm, "radius": 3.18 * mm});
            skCircle(sketch, "E37.11.1.0", {"center": v(509.92, -276.96) * mm, "radius": 3.18 * mm});
            skCircle(sketch, "E37.12.0.0", {"center": v(586.12, 256.44) * mm, "radius": 3.18 * mm});
            skCircle(sketch, "E37.12.1.0", {"center": v(586.12, -276.96) * mm, "radius": 3.18 * mm});
            skCircle(sketch, "E37.13.0.0", {"center": v(662.32, 256.44) * mm, "radius": 3.18 * mm});
            skCircle(sketch, "E37.13.1.0", {"center": v(662.32, -276.96) * mm, "radius": 3.18 * mm});
            skCircle(sketch, "E37.14.0.0", {"center": v(738.52, 256.44) * mm, "radius": 3.18 * mm});
            skCircle(sketch, "E37.14.1.0", {"center": v(738.52, -276.96) * mm, "radius": 3.18 * mm});
            skCircle(sketch, "E37.15.0.0", {"center": v(814.72, 256.44) * mm, "radius": 3.18 * mm});
            skCircle(sketch, "E37.15.1.0", {"center": v(814.72, -276.96) * mm, "radius": 3.18 * mm});
            skCircle(sketch, "E37.16.0.0", {"center": v(890.92, 256.44) * mm, "radius": 3.18 * mm});
            skCircle(sketch, "E37.16.1.0", {"center": v(890.92, -276.96) * mm, "radius": 3.18 * mm});
            skCircle(sketch, "E37.17.0.0", {"center": v(967.12, 256.44) * mm, "radius": 3.18 * mm});
            skCircle(sketch, "E37.17.1.0", {"center": v(967.12, -276.96) * mm, "radius": 3.18 * mm});
            skCircle(sketch, "E37.18.0.0", {"center": v(1043.32, 256.44) * mm, "radius": 3.18 * mm});
            skCircle(sketch, "E37.18.1.0", {"center": v(1043.32, -276.96) * mm, "radius": 3.18 * mm});
            skCircle(sketch, "E37.19.0.0", {"center": v(1119.52, 256.44) * mm, "radius": 3.18 * mm});
            skCircle(sketch, "E37.19.1.0", {"center": v(1119.52, -276.96) * mm, "radius": 3.18 * mm});
            skLineSegment(sketch, "E37.direction1", {"start": v(-328.28, 256.44) * mm, "end": v(-252.08, 256.44) * mm, "construction": true});
            skLineSegment(sketch, "E37.direction2", {"start": v(-328.28, 256.44) * mm, "end": v(-328.28, -276.96) * mm, "construction": true});
            skSolve(sketch);
        }
        {
            var Q0;
            Q0 = qSketchRegion(id + "F26", true);
            extrude(context, id + "F27", {"entities" : qUnion([Q0]), "operationType" : NewBodyOperationType.REMOVE, "oppositeDirection" : true, "depth" : 9.52 * mm});
        }
        {
            var Q0;
            {var subQ0=sQuery(id+"F0.wireOp",EDGE,"E0.top");var subQ1=sQuery(id+"F2.wireOp",EDGE,"E2.0");var subQ2=sQuery(id+"F0.wireOp",EDGE,"E0.left");Q0=makeQuery(id+"F3.boolean.opBoolean","SPLIT",FACE,{"disambiguationData":[TD([makeQuery(id+"F3.opExtrude","SWEPT_FACE",FACE,{"disambiguationData":[OSD([subQ1]),TDD([makeQuery(id+"F2.imprint","IMPRINT",EDGE,{"disambiguationData":[TD([[makeQuery(id+"F2.imprint","INTERSECT",VERTEX,{"derivedFrom":[makeQuery(id+"F1.opExtrude","CAP_EDGE",EDGE,{"disambiguationData":[OSD([subQ2])],"isStart":false}),subQ1]}),-1.0]])],"derivedFrom":subQ1})])]})])],"derivedFrom":makeQuery(id+"F1.opExtrude","CAP_FACE",FACE,{"disambiguationData":[OSD([sQuery(id+"F0.wireOp",EDGE,"E0.bottom"),subQ0,subQ2,sQuery(id+"F0.wireOp",EDGE,"E0.right")])],"isStart":false})});}
            var sketch = newSketch(context, id + "F28", { "sketchPlane" : qUnion([Q0])});
            skLineSegment(sketch, "E38.bottom", {"start": v(-620.38, 351.69) * mm, "end": v(-404.48, 351.69) * mm});
            skLineSegment(sketch, "E38.top", {"start": v(-620.38, -67.41) * mm, "end": v(-404.48, -67.41) * mm});
            skLineSegment(sketch, "E38.left", {"start": v(-620.38, 351.69) * mm, "end": v(-620.38, -67.41) * mm});
            skLineSegment(sketch, "E38.right", {"start": v(-404.48, 351.69) * mm, "end": v(-404.48, -67.41) * mm});
            skSolve(sketch);
        }
        {
            var Q0;
            Q0 = qSketchRegion(id + "F28", true);
            extrude(context, id + "F29", {"entities" : qUnion([Q0]), "operationType" : NewBodyOperationType.REMOVE, "oppositeDirection" : true, "depth" : 12.7 * mm});
        }
        {
            var Q0;
            {var subQ0=sQuery(id+"F0.wireOp",EDGE,"E0.bottom");var subQ3=sQuery(id+"F2.wireOp",EDGE,"E1.0");var subQ5=sQuery(id+"F2.wireOp",EDGE,"E4.0");var subQ6=makeQuery(id+"F2.imprint","INTERSECT",VERTEX,{"derivedFrom":[subQ3,subQ5]});Q0=makeQuery(id+"F3.boolean.opBoolean","SPLIT",FACE,{"disambiguationData":[TD([makeQuery(id+"F3.opExtrude","SWEPT_FACE",FACE,{"disambiguationData":[OSD([subQ3]),TDD([makeQuery(id+"F2.imprint","IMPRINT",EDGE,{"disambiguationData":[TD([[subQ6,-1.0]])],"derivedFrom":subQ3})])]})])],"derivedFrom":makeQuery(id+"F1.opExtrude","CAP_FACE",FACE,{"disambiguationData":[OSD([subQ0,sQuery(id+"F0.wireOp",EDGE,"E0.top"),sQuery(id+"F0.wireOp",EDGE,"E0.left"),sQuery(id+"F0.wireOp",EDGE,"E0.right")])],"isStart":false})});}
            var sketch = newSketch(context, id + "F30", { "sketchPlane" : qUnion([Q0])});
            skLineSegment(sketch, "E39.0", {"start": v(-582.28, -80.11) * mm, "end": v(-391.78, -80.11) * mm});
            skLineSegment(sketch, "E40.0", {"start": v(-582.28, -92.81) * mm, "end": v(-379.08, -92.81) * mm});
            skLineSegment(sketch, "E41.0", {"start": v(-391.78, 332.64) * mm, "end": v(-391.78, -80.11) * mm});
            skLineSegment(sketch, "E42.0", {"start": v(-379.08, 332.64) * mm, "end": v(-379.08, -92.81) * mm});
            skSolve(sketch);
        }
        {
            var Q0;
            {var subQ3=sQuery(id+"F30.wireOp",EDGE,"E39.0");Q0=makeQuery(id+"F30.imprint","IMPRINT",FACE,{"disambiguationData":[TD([[makeQuery(id+"F30.imprint","IMPRINT",EDGE,{"derivedFrom":subQ3}),-1.0]])]});}
            extrude(context, id + "F31", {"entities" : qUnion([Q0]), "operationType" : NewBodyOperationType.REMOVE, "oppositeDirection" : true, "depth" : 6.35 * mm});
        }
        {
            var Q0;
            Q0=qCreatedBy(makeId("Front.planeOp"),FACE);
            var sketch = newSketch(context, id + "F32", { "sketchPlane" : qUnion([Q0])});
            skLineSegment(sketch, "E43.bottom", {"start": v(171.13, -627.77) * mm, "end": v(755.33, -627.77) * mm});
            skLineSegment(sketch, "E43.top", {"start": v(171.13, -348.37) * mm, "end": v(755.33, -348.37) * mm});
            skLineSegment(sketch, "E43.left", {"start": v(171.13, -627.77) * mm, "end": v(171.13, -348.37) * mm});
            skLineSegment(sketch, "E43.right", {"start": v(755.33, -627.77) * mm, "end": v(755.33, -348.37) * mm});
            skSolve(sketch);
        }
        {
            var Q0;
            Q0 = qSketchRegion(id + "F32", true);
            extrude(context, id + "F33", {"entities" : qUnion([Q0]), "depth" : 12.7 * mm});
        }
        {
            var Q0;
            Q0=makeQuery(id+"F17.opExtrude","CAP_FACE",FACE,{"disambiguationData":[OSD([sQuery(id+"F16.wireOp",EDGE,"E24.bottom"),sQuery(id+"F16.wireOp",EDGE,"E24.top"),sQuery(id+"F16.wireOp",EDGE,"E24.left"),sQuery(id+"F16.wireOp",EDGE,"E24.right")])],"isStart":false});
            var sketch = newSketch(context, id + "F34", { "sketchPlane" : qUnion([Q0])});
            skLineSegment(sketch, "E44.0", {"start": v(1404.52, -833.85) * mm, "end": v(1404.52, 1299.75) * mm});
            skLineSegment(sketch, "E45.0", {"start": v(1417.22, -833.85) * mm, "end": v(1417.22, 1299.75) * mm});
            skSolve(sketch);
        }
        {
            var Q0;
            {var subQ0=sQuery(id+"F34.wireOp",EDGE,"E44.0");Q0=makeQuery(id+"F34.imprint","IMPRINT",FACE,{"disambiguationData":[TD([[makeQuery(id+"F34.imprint","IMPRINT",EDGE,{"derivedFrom":subQ0}),-1.0]])]});}
            extrude(context, id + "F35", {"entities" : qUnion([Q0]), "operationType" : NewBodyOperationType.REMOVE, "oppositeDirection" : true, "depth" : 6.35 * mm});
        }
        {
            var Q0;
            Q0=makeQuery(id+"F17.opExtrude","CAP_FACE",FACE,{"disambiguationData":[OSD([sQuery(id+"F16.wireOp",EDGE,"E26.bottom"),sQuery(id+"F16.wireOp",EDGE,"E26.top"),sQuery(id+"F16.wireOp",EDGE,"E26.left"),sQuery(id+"F16.wireOp",EDGE,"E26.right")])],"isStart":false});
            var sketch = newSketch(context, id + "F36", { "sketchPlane" : qUnion([Q0])});
            skLineSegment(sketch, "E46.0", {"start": v(2030.11, -1462.53) * mm, "end": v(1496.71, -1462.53) * mm});
            skLineSegment(sketch, "E47.0", {"start": v(2030.11, -1449.83) * mm, "end": v(1496.71, -1449.83) * mm});
            skSolve(sketch);
        }
        {
            var Q0;
            {var subQ0=sQuery(id+"F36.wireOp",EDGE,"E46.0");Q0=makeQuery(id+"F36.imprint","IMPRINT",FACE,{"disambiguationData":[TD([[makeQuery(id+"F36.imprint","IMPRINT",EDGE,{"derivedFrom":subQ0}),-1.0]])]});}
            extrude(context, id + "F37", {"entities" : qUnion([Q0]), "operationType" : NewBodyOperationType.REMOVE, "oppositeDirection" : true, "depth" : 6.35 * mm});
        }
        {
            var Q0;
            Q0=makeQuery(id+"F17.opExtrude","CAP_FACE",FACE,{"disambiguationData":[OSD([sQuery(id+"F16.wireOp",EDGE,"E25.bottom"),sQuery(id+"F16.wireOp",EDGE,"E25.top"),sQuery(id+"F16.wireOp",EDGE,"E25.left"),sQuery(id+"F16.wireOp",EDGE,"E25.right")])],"isStart":false});
            var sketch = newSketch(context, id + "F38", { "sketchPlane" : qUnion([Q0])});
            skLineSegment(sketch, "E48.0", {"start": v(1542.63, 1798.51) * mm, "end": v(1009.23, 1798.51) * mm});
            skLineSegment(sketch, "E49.0", {"start": v(1542.63, 1811.21) * mm, "end": v(1009.23, 1811.21) * mm});
            skSolve(sketch);
        }
        {
            var Q0;
            {var subQ0=sQuery(id+"F38.wireOp",EDGE,"E48.0");Q0=makeQuery(id+"F38.imprint","IMPRINT",FACE,{"disambiguationData":[TD([[makeQuery(id+"F38.imprint","IMPRINT",EDGE,{"derivedFrom":subQ0}),-1.0]])]});}
            extrude(context, id + "F39", {"entities" : qUnion([Q0]), "operationType" : NewBodyOperationType.REMOVE, "oppositeDirection" : true, "depth" : 6.35 * mm});
        }
    });
